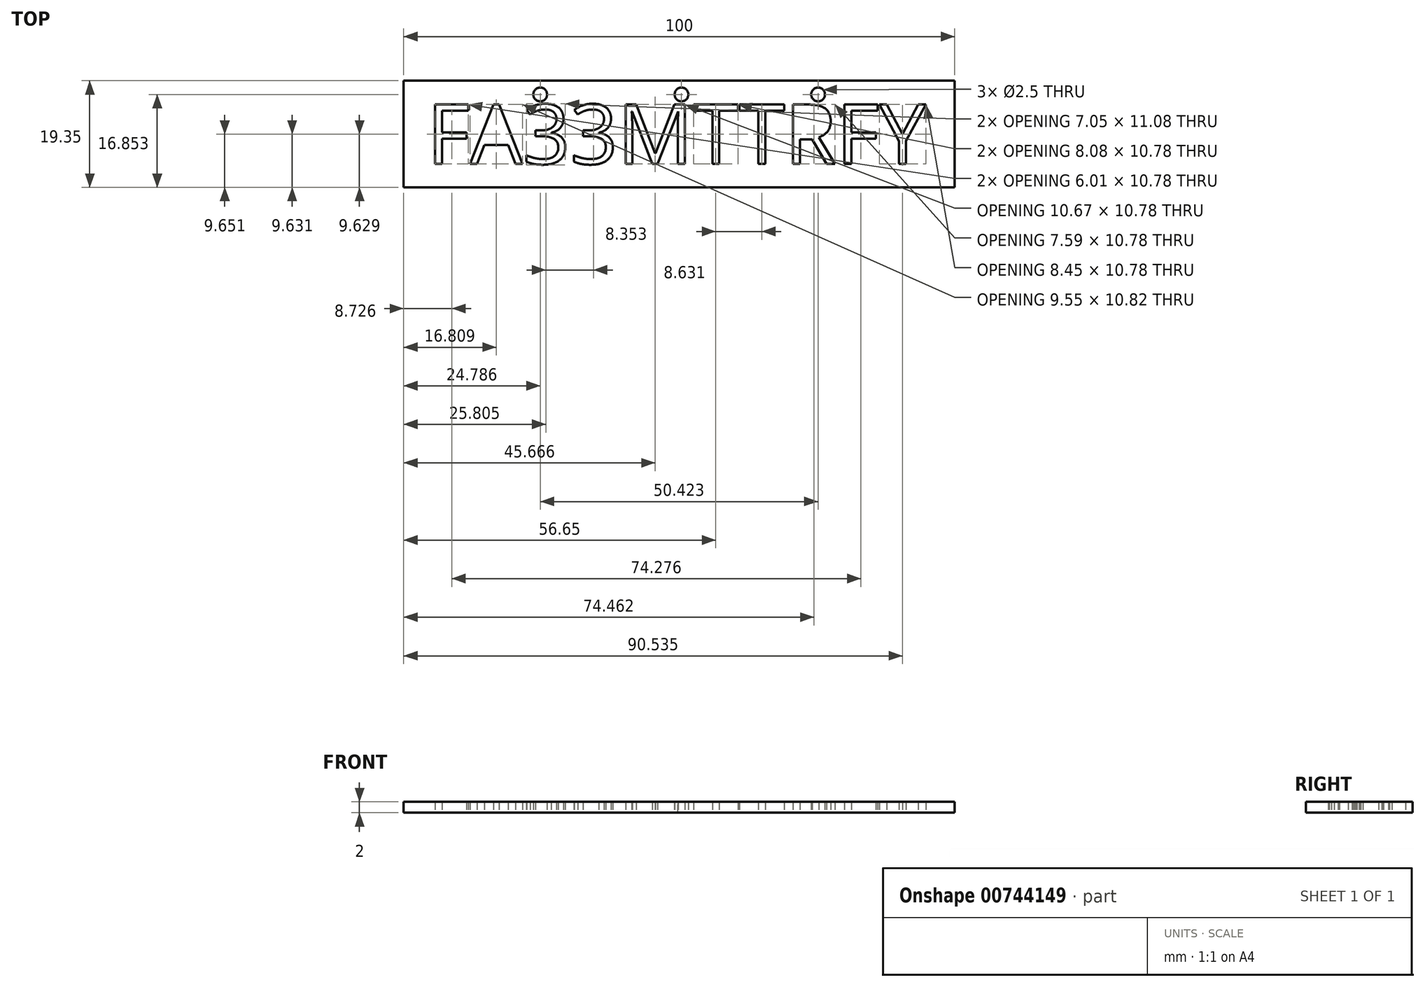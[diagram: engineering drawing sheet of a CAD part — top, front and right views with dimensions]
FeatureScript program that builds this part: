
annotation { "Feature Type Name" : "Feature", "Feature Type Description" : "" }
export const myFeature = defineFeature(function(context is Context, id is Id, definition is map)
    precondition{}
    {
        {
            var Q0;
            Q0=qCreatedBy(makeId("Top.planeOp"),FACE);
            var sketch = newSketch(context, id + "F0", { "sketchPlane" : qUnion([Q0])});
            skText(sketch, "E0", { "text": "FA33MTTRFY", "fontName": "OpenSans-Regular.ttf"});
            skLineSegment(sketch, "E1", {"start": v(91.51, -10.87) * mm, "end": v(95.76, -15.11) * mm});
            skLineSegment(sketch, "E2", {"start": v(0, 0) * mm, "end": v(-4.24, 4.24) * mm});
            skLineSegment(sketch, "E3.bottom", {"start": v(-4.24, 4.24) * mm, "end": v(95.76, 4.24) * mm});
            skLineSegment(sketch, "E3.top", {"start": v(-4.24, -15.11) * mm, "end": v(95.76, -15.11) * mm});
            skLineSegment(sketch, "E3.left", {"start": v(-4.24, 4.24) * mm, "end": v(-4.24, -15.11) * mm});
            skLineSegment(sketch, "E3.right", {"start": v(95.76, 4.24) * mm, "end": v(95.76, -15.11) * mm});
            skLineSegment(sketch, "E4", {"start": v(-4.24, -20.76) * mm, "end": v(95.76, -20.76) * mm, "construction": true});
            skPoint(sketch, "E4.startSnap0", {"position": v(-2.12, -20.76) * mm});
            skLineSegment(sketch, "E5", {"start": v(95.76, 4.24) * mm, "end": v(95.76, -20.76) * mm, "construction": true});
            skLineSegment(sketch, "E6", {"start": v(95.76, 1.74) * mm, "end": v(-4.24, 1.74) * mm, "construction": true});
            skLineSegment(sketch, "E7", {"start": v(84.7, 4.24) * mm, "end": v(84.7, 1.74) * mm, "construction": true});
            skCircle(sketch, "E8", {"center": v(70.97, 1.74) * mm, "radius": 1.25 * mm});
            skCircle(sketch, "E9", {"center": v(46.18, 1.74) * mm, "radius": 1.25 * mm});
            skCircle(sketch, "E10", {"center": v(20.55, 1.74) * mm, "radius": 1.25 * mm});
            skLineSegment(sketch, "E11", {"start": v(70.97, 1.74) * mm, "end": v(95.76, 1.74) * mm, "construction": true});
            skLineSegment(sketch, "E12", {"start": v(46.18, 1.74) * mm, "end": v(70.97, 1.74) * mm, "construction": true});
            skLineSegment(sketch, "E13", {"start": v(20.55, 1.74) * mm, "end": v(-4.24, 1.74) * mm, "construction": true});
            const initialGuessF0  = {"E0": [0, -0.01087, 1, 0, 0.01087]};
            skSetInitialGuess(sketch, initialGuessF0);
            skSolve(sketch);
        }
        {
            var Q0;
            Q0=makeQuery(id+"F0.imprint","IMPRINT",FACE,{"disambiguationData":[TD([[makeQuery(id+"F0.imprint","IMPRINT",EDGE,{"derivedFrom":sQuery(id+"F0.wireOp",EDGE,"E0.sketch_text.stroke-0")}),1.0]])]});
            extrude(context, id + "F1", {"entities" : qUnion([Q0]), "depth" : 2 * mm, "offsetDistance" : 25 * mm});
        }
        {
            var Q0;
            Q0 = qSketchRegion(id + "F0", true);
            extrude(context, id + "F2", {"entities" : qUnion([Q0]), "operationType" : NewBodyOperationType.REMOVE, "oppositeDirection" : true, "depth" : 25 * mm, "offsetDistance" : 25 * mm});
        }
    });
